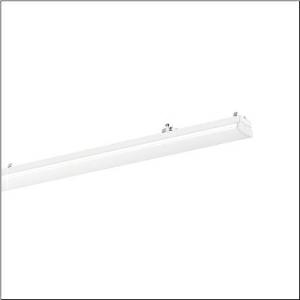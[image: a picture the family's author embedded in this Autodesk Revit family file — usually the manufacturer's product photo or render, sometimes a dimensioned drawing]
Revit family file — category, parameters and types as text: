
# Revit family: licross_11_recessed_opal_ho_51tl1dcn4cxm
name_source: partatom
category: Lighting Fixtures
units: mm (PartAtom-declared; Revit-internal decimal feet)

## family parameters
Cut with Voids When Loaded = No
Host = Face
Light Source = No
Part Type = Normal
Room Calculation Point = No
Round Connector Dimension = Use Diameter
Shared = No

## types (1)
- --- (1 x LED, 12370 lm, 66.5 W, 4000K)
    Apparent Load = 67 VA
    CIE Flux Codes = 44 73 91 87 100
    Color Rendering = 80
    Color Temperature = 4000K
    Default Elevation = 1800 mm
    Description = Licross 11 recessed opal HO, luminaire insert, of sheet steel, coil coated, white, length: 1.500mm, width: 76mm, height: 87mm, LED rated luminous flux: 12.370lm, light colour: 840, SDCM (Standard Deviation of Colour Matching)MacAdam ≤ 2 SDCM (initial), control gear: ON/OFF Multilumen, CLOi, with plug, 3-pole, with phase selection, mains connection: 220..240V, AC, 50/60Hz, start of lifetime: 67W, end of service life: 75W, internal wiring halogen-free, primary optical cover: cover, of PMMA, light emission: direct with ceiling illumination distribution, primary light characteristic: symmetric, protection rating (complete): IP40, insulation class (complete): insulation class I (protective earthing), certification: CE, ENEC, VDE, UKCA, protection symbol: D if used in an environment without relevant dust loads with corresponding accessories, impact resistance: IK06, permissible ambient temperature for indoor applications: -35..+35°C, corresponds to IFS (International Featured Standards) requirements for safety and quality in the food industry, reducing of maximum allowable ambient temperature of 5°C with ceiling mounting, LABS conformity tested according to VDMA 24364:2018-05, The light source and the operating device comply with the requirements of the Ecodesign Regulation (EU) 2019/2020 and are replaceable in accordance with this regulation, packaging unit: 1 piece
    Height = 83 mm
    Lamp = 1 x LED
    Lamp Light Flux = 12370 lm
    Lamp Power = 66.5 W
    Lamp count = 1
    Length = 1500 mm
    Luminous efficacy = 186 lm/W
    Manufacturer = Siteco
    ModVariant = No
    Model = 51TL1DCN4CXM
    Mounting Place = Ceiling
    Mounting Type = Pendant
    Number of Poles = 1
    OnlyDefault = Yes
    Power Factor = 1
    Product Name = Licross 11 recessed opal HO
    Product group = luminaire insert | ceiling pendant
    ProductGroupID = 901
    Protection Class = Protection class I
    Protection Degree = IP 40
    RLX_Detail_Level = 1
    RLX_Emergency_Light_Flux = 0 lm
    RLX_Emergency_Type = 0
    RLX_Emergency_Type_DB = No
    RlxData = <blob elided: 24985 chars, md5=88a54d73>
    Socket = socket
    Standby Power = 0 W
    System Light Flux = 12370 lm
    System Power = 67 W
    Type Comments = factory setting: luminous flux: 100 % | (A | C | E) | 156 mA
    Type Image = l_1313666.jpg
    URL = http://relux.com
    VarID = @adj_000193
    Voltage = 0 V
    Weight = 0.00 kg
    Width = 76 mm

## geometry (parser evidence)
native form markers: Blend x4, Sweep x11
no freeform markers — native parametric forms only
